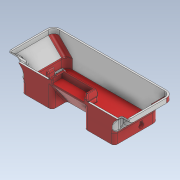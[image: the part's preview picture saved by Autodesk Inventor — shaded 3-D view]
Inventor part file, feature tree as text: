
AUTODESK INVENTOR PART (.ipt)
format: ipt  version: 2022.1 (Build 261234020, 234B)  size: 2,060,288 bytes
history: native  units: mm
features: fillet x23, delete_face x13, sketch x11, extrude x10, other x8, projected_geometry x8, chamfer x5, reference x5, mirror x4, plane x2, direct_edit x2, move_body x2, hole x1
ambient origin geometry x8: Origin, YZ Plane, XZ Plane, XY Plane, X Axis, Y Axis, Z Axis, Center Point
bodies: Volumenkörper1 (feature_tree)
feature tree (94):
  other  "Bucket_SRC_1.iam"
  other  "Bucket_Rama.ipt:1"
  other  "Brush_Holder.ipt:1"
  delete_face  "Fläche löschen1"
  extrude  "Extrusion1"  Depth=2.0mm TaperAngle=0.0deg
  plane  "Arbeitsebene1"
  mirror  "Spiegeln1"
  delete_face  "Fläche löschen2"
  delete_face  "Fläche löschen3"
  delete_face  "Fläche löschen4"
  delete_face  "Fläche löschen5"
  chamfer  "Fase1"  Distance=0.4mm Angle=45.0deg
  extrude  "Extrusion2"  Depth=3.0mm
  delete_face  "Fläche löschen6"
  fillet  "Rundung1"  Radius=2.0mm
  fillet  "Rundung2"  Radius=3.0mm
  fillet  "Rundung3"  Radius=2.0mm
  fillet  "Rundung4"  Radius=2.0mm
  fillet  "Rundung5"  Radius=4.0mm
  fillet  "Rundung6"  Radius=2.0mm
  fillet  "Rundung7"  Radius=4.0mm
  fillet  "Rundung8"  Radius=4.0mm
  fillet  "Rundung9"  Radius=2.0mm
  fillet  "Rundung10"  Radius=2.0mm
  direct_edit  "Direktbearbeitung1"
  chamfer  "Fase2"  [1 undecoded]
  chamfer  "Fase3"  Distance=1.0mm Angle=45.0deg
  sketch  "Skizze4"  dims[d19=4.0mm d20=0.0mm d21=0.0mm d22=-3.0mm d25=1.0mm d26=2.0mm d27=45.0deg]
  delete_face  "Fläche löschen7"
  extrude  "Extrusion4"  Depth=6.06mm
  fillet  "Rundung13"  Radius=12.12mm
  fillet  "Rundung14"  Radius=12.12mm
  hole  "Bohrung1"  [1 undecoded]
  sketch  "Skizze6"  dims[d39=10.0mm d40=0.0mm d41=1.0mm]
  plane  "Arbeitsebene2"
  extrude  "Extrusion5"  Depth=0.6mm
  extrude  "Extrusion6"  Depth=15.600003mm
  extrude  "Extrusion7"  Depth=10.0mm TaperAngle=0.0deg
  mirror  "Spiegeln2"
  delete_face  "Fläche löschen8"
  direct_edit  "Direktbearbeitung2"
  fillet  "Rundung15"  Radius=2.0mm
  fillet  "Rundung16"  Radius=2.0mm
  chamfer  "Fase5"  Distance=10.0mm
  chamfer  "Fase6"  Distance=10.0mm
  fillet  "Rundung17"  Radius=2.0mm
  fillet  "Rundung18"  Radius=4.0mm
  extrude  "Extrusion8"  Depth=3.0mm TaperAngle=45.0deg
  mirror  "Spiegeln3"
  delete_face  "Fläche löschen9"
  delete_face  "Fläche löschen10"
  delete_face  "Fläche löschen11"
  extrude  "Extrusion9"  Depth=2.0mm
  extrude  "Extrusion10"  Depth=4.0mm
  extrude  "Extrusion11"  Depth=10.0mm TaperAngle=0.0deg
  mirror  "Spiegeln4"
  fillet  "Rundung19"  Radius=10.0mm
  fillet  "Rundung20"  Radius=1.4mm
  delete_face  "Fläche löschen12"
  delete_face  "Fläche löschen13"
  fillet  "Rundung22"  Radius=10.0mm
  fillet  "Rundung23"  Radius=0.4mm
  fillet  "Rundung24"  Radius=10.0mm
  fillet  "Rundung25"  Radius=1.34mm
  fillet  "Rundung26"  Radius=2.0mm
  sketch  "Skizze1"  dims[d0=10.0mm d1=2.0mm d2=0.0mm d3=0.4mm d4=2.0mm d5=45.0deg]
  projected_geometry  "Projizierte Kontur1"
  sketch  "Skizze2"  dims[d6=3.0mm d7=3.0mm d8=2.0mm d9=0.0mm d10=3.0mm d11=2.0mm d12=2.0mm d13=4.0mm d14=2.0mm d15=4.0mm d16=4.0mm d17=2.0mm d18=2.0mm]
  projected_geometry  "Projizierte Kontur2"
  projected_geometry  "Projizierte Kontur3"
  reference  "Referenz1"
  reference  "Referenz2"
  sketch  "Skizze5"  dims[d28=0.4mm d29=2.0mm d30=45.0deg d36=6.06mm d37=12.12mm d38=12.12mm]
  reference  "Referenz3"
  reference  "Referenz4"
  projected_geometry  "Projizierte Kontur6"
  reference  "Referenz5"
  sketch  "Skizze7"  dims[d42=2.0mm]
  sketch  "Skizze8"  dims[d43=6.12mm d44=6.0mm d45=4.0mm d46=2.0mm d47=90.0deg d48=3.2mm d49=0.0mm d51=0.6mm]
  projected_geometry  "Projizierte Kontur7"
  sketch  "Skizze9"  dims[d52=1.05mm d53=15.600003mm]
  projected_geometry  "Projizierte Kontur8"
  sketch  "Skizze10"  dims[d54=15.600003mm d55=10.0mm d56=0.0mm d57=2.0mm d58=2.0mm d59=10.0mm d60=0.0mm d61=10.0mm d62=0.0mm]
  sketch  "Skizze11"  dims[d63=0.0mm d64=0.0mm d65=4.0mm d66=2.0mm d67=4.0mm]
  projected_geometry  "Projizierte Kontur9"
  sketch  "Skizze12"  dims[d68=2.0mm d69=2.0mm d70=45.0deg d71=3.0mm d72=2.0mm d73=45.0deg d74=2.0mm d75=4.0mm d76=10.0mm d77=0.0mm d78=10.0mm d79=0.0mm d80=1.4mm d81=10.0mm d82=0.0mm d83=0.4mm d84=10.0mm d85=0.0mm d86=1.34mm d87=2.0mm d89=4.0mm d90=2.0mm d91=4.0mm d92=2.0mm d93=4.0mm]
  projected_geometry  "Projizierte Kontur10"
  move_body  "Verschieben1"
  other  "<userpath>\Desktop\RAMA_SBNG\BedPan\Ramabed.iam"
  other  "Ramabed.iam"
  other  "Ramabed wago mount:1"
  other  "1_Kinematic:1"
  other  "ISO 7380-1 M3 x 8:2"
  move_body  "Verschieben2"
note: 2 required parameter values undecoded (feature->parameter linkage not recoverable at this tier; creation-order binding heuristic only, values carry confidence <= 0.55)
